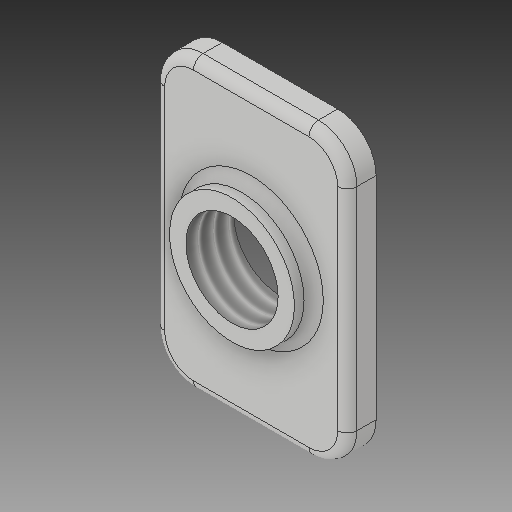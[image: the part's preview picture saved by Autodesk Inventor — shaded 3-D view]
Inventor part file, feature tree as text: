
AUTODESK INVENTOR PART (.ipt)
format: ipt  version: 2018 (Build 220112000, 112)  size: 164,352 bytes
history: native  units: mm
features: other x3, sketch x2
ambient origin geometry x8: Origin, YZ Plane, XZ Plane, XY Plane, X Axis, Y Axis, Z Axis, Center Point
bodies: Solid1 (feature_tree)
feature tree (5):
  other  "M5 Tee Nut_MIR_MIR_MIR.ipt"
  other  "Solid1::M5 Tee Nut_MIR_MIR_MIR.ipt"
  other  "TaggingFeature1"
  sketch  "Sketch1"  dims[d0=10.0mm]
  sketch  "Sketch2"
